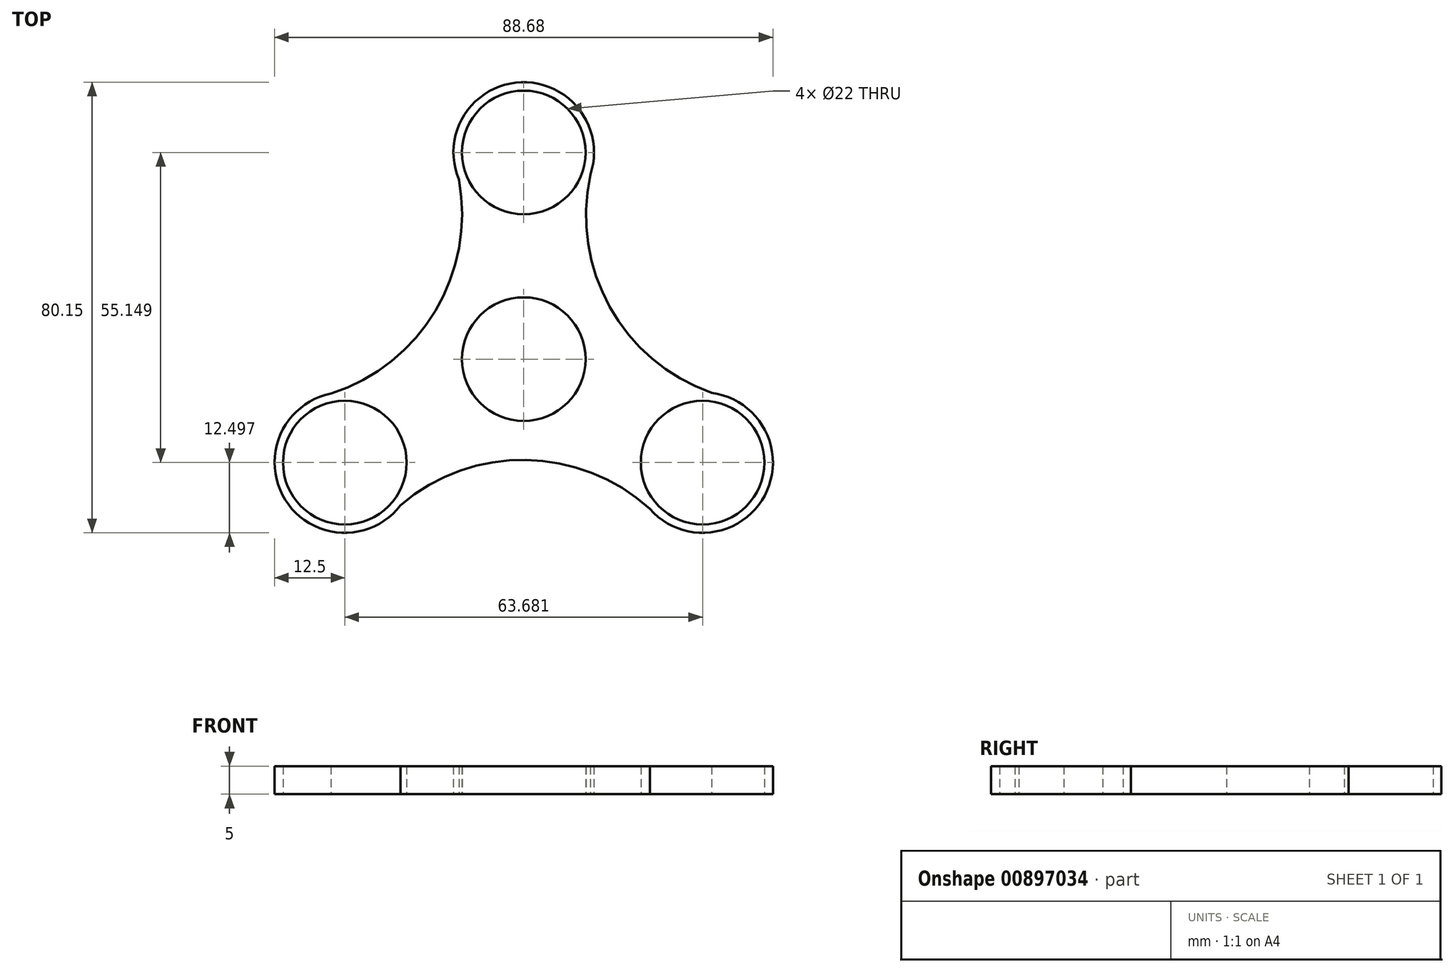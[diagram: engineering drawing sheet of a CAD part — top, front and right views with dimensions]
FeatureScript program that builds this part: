
annotation { "Feature Type Name" : "Feature", "Feature Type Description" : "" }
export const myFeature = defineFeature(function(context is Context, id is Id, definition is map)
    precondition{}
    {
        {
            var Q0;
            Q0=qCreatedBy(makeId("Top.planeOp"),FACE);
            var sketch = newSketch(context, id + "F0", { "sketchPlane" : qUnion([Q0])});
            skCircle(sketch, "E0", {"center": v(0, 0) * mm, "radius": 11 * mm});
            skCircle(sketch, "E1", {"center": v(0, 36.77) * mm, "radius": 11 * mm});
            skCircle(sketch, "E2.1.0", {"center": v(-31.84, -18.38) * mm, "radius": 11 * mm});
            skCircle(sketch, "E2.2.0", {"center": v(31.84, -18.38) * mm, "radius": 11 * mm});
            skCircle(sketch, "E3", {"center": v(0, 36.77) * mm, "radius": 12.5 * mm});
            skCircle(sketch, "E4.1.0", {"center": v(-31.84, -18.38) * mm, "radius": 12.5 * mm});
            skCircle(sketch, "E4.2.0", {"center": v(31.84, -18.38) * mm, "radius": 12.5 * mm});
            skArc(sketch, "E5", {"start": v(22.45, -26.64) * mm, "mid": v(-1.52, -17.94) * mm, "end": v(-24.67, -28.62) * mm});
            skArc(sketch, "E6.1.0", {"start": v(11.84, 32.76) * mm, "mid": v(16.3, 7.66) * mm, "end": v(37.12, -7.05) * mm});
            skArc(sketch, "E6.2.0", {"start": v(-34.3, -6.13) * mm, "mid": v(-14.78, 10.28) * mm, "end": v(-12.45, 35.68) * mm});
            skSolve(sketch);
        }
        {
            var Q0;
            Q0 = qSketchRegion(id + "F0", true);
            extrude(context, id + "F1", {"entities" : qUnion([Q0]), "depth" : 5 * mm, "offsetDistance" : 25 * mm});
        }
    });
